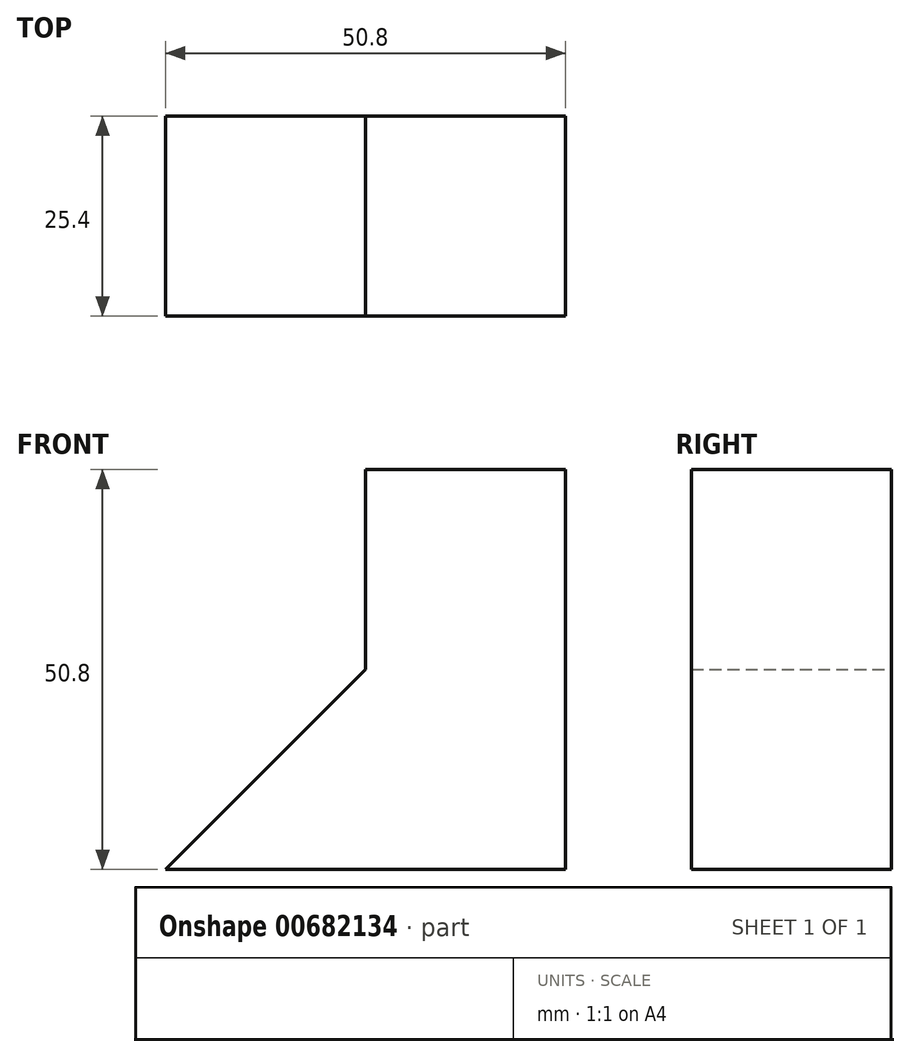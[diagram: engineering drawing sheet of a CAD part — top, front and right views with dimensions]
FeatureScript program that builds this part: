
annotation { "Feature Type Name" : "Feature", "Feature Type Description" : "" }
export const myFeature = defineFeature(function(context is Context, id is Id, definition is map)
    precondition{}
    {
        {
            var Q0;
            Q0=qCreatedBy(makeId("Front.planeOp"),FACE);
            var sketch = newSketch(context, id + "F0", { "sketchPlane" : qUnion([Q0])});
            skLineSegment(sketch, "E0", {"start": v(-35.3, 23.67) * mm, "end": v(-35.3, 49.07) * mm});
            skLineSegment(sketch, "E1", {"start": v(-35.3, 49.07) * mm, "end": v(-9.9, 49.07) * mm});
            skLineSegment(sketch, "E2", {"start": v(-9.9, 49.07) * mm, "end": v(-9.9, -1.73) * mm});
            skLineSegment(sketch, "E3", {"start": v(-9.9, -1.73) * mm, "end": v(-60.7, -1.73) * mm});
            skLineSegment(sketch, "E4", {"start": v(-60.7, -1.73) * mm, "end": v(-35.3, 23.67) * mm});
            skSolve(sketch);
        }
        {
            var Q0;
            Q0 = qSketchRegion(id + "F0", true);
            extrude(context, id + "F1", {"entities" : qUnion([Q0]), "depth" : 25.4 * mm, "offsetDistance" : 25.4 * mm});
        }
    });
